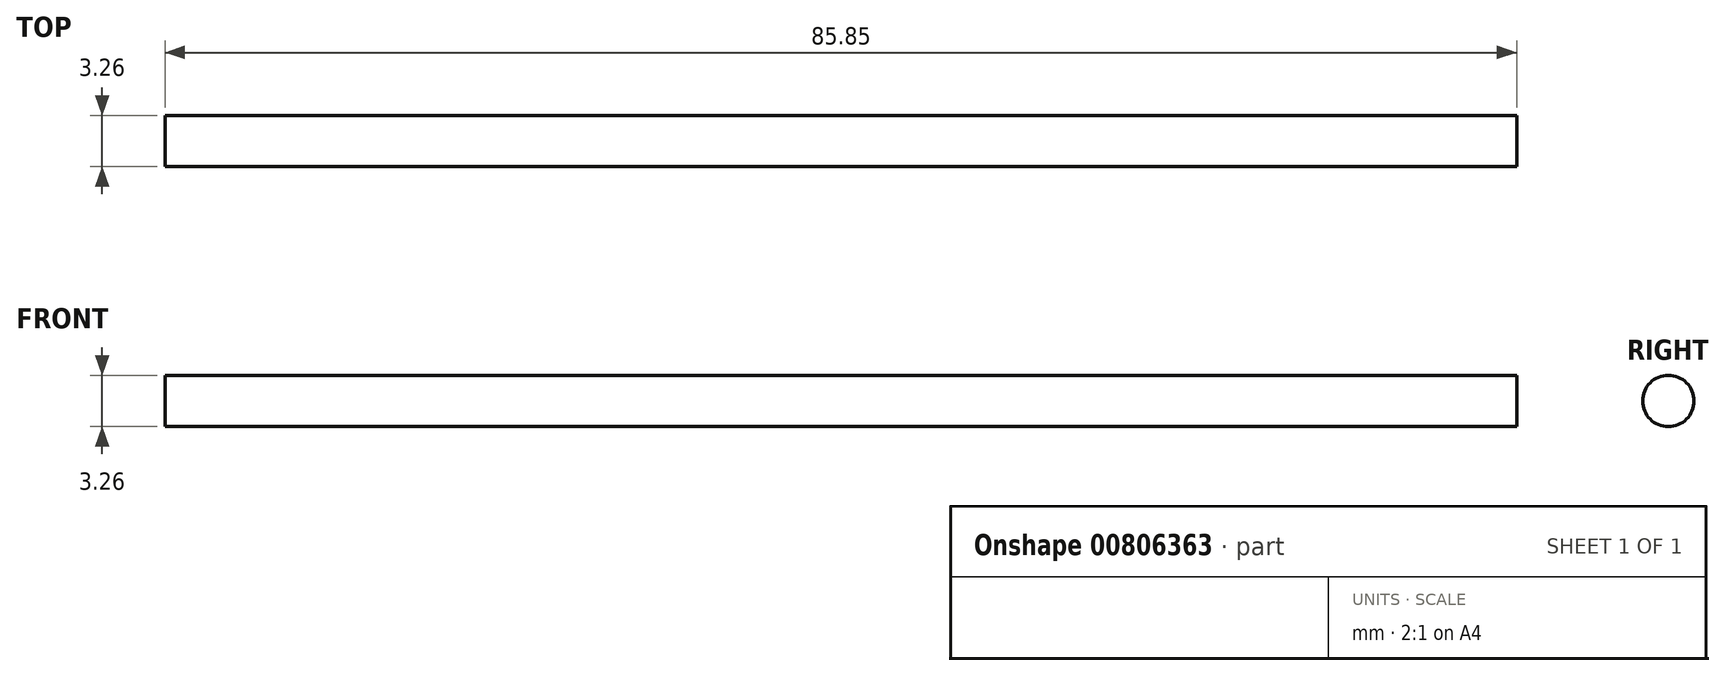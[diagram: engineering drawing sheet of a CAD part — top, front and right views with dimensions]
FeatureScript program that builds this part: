
annotation { "Feature Type Name" : "Feature", "Feature Type Description" : "" }
export const myFeature = defineFeature(function(context is Context, id is Id, definition is map)
    precondition{}
    {
        {
            var Q0;
            Q0=qCreatedBy(makeId("Right.planeOp"),FACE);
            var sketch = newSketch(context, id + "F0", { "sketchPlane" : qUnion([Q0])});
            skCircle(sketch, "E0", {"center": v(0, 0) * mm, "radius": 1.63 * mm});
            skSolve(sketch);
        }
        {
            var Q0;
            Q0 = qSketchRegion(id + "F0", true);
            extrude(context, id + "F1", {"entities" : qUnion([Q0]), "depth" : 85.85 * mm, "offsetDistance" : 25.4 * mm});
        }
    });
